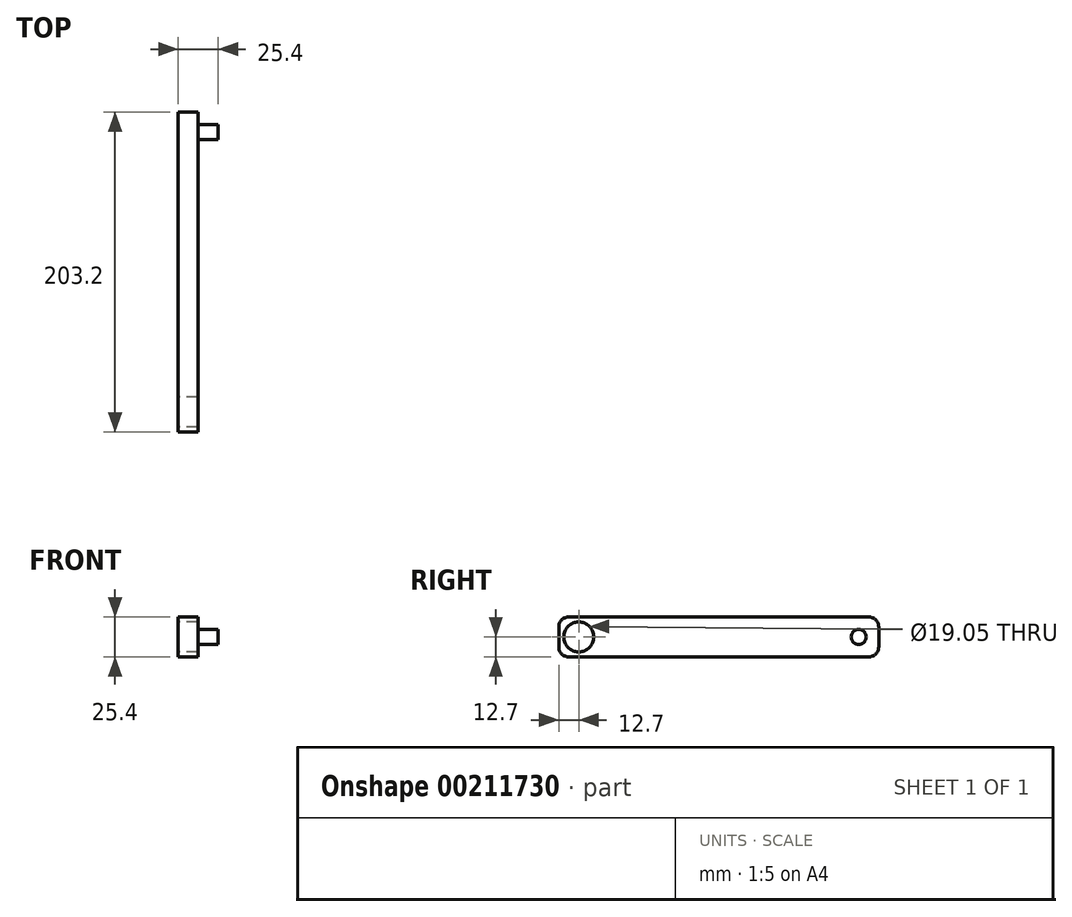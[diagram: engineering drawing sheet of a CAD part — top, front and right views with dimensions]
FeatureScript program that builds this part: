
annotation { "Feature Type Name" : "Feature", "Feature Type Description" : "" }
export const myFeature = defineFeature(function(context is Context, id is Id, definition is map)
    precondition{}
    {
        {
            var Q0;
            Q0=qCreatedBy(makeId("Right.planeOp"),FACE);
            var sketch = newSketch(context, id + "F0", { "sketchPlane" : qUnion([Q0])});
            skLineSegment(sketch, "E0.bottom", {"start": v(95.25, 12.7) * mm, "end": v(-95.25, 12.7) * mm});
            skLineSegment(sketch, "E0.top", {"start": v(95.25, -12.7) * mm, "end": v(-95.25, -12.7) * mm});
            skLineSegment(sketch, "E0.left", {"start": v(101.6, 6.35) * mm, "end": v(101.6, -6.35) * mm});
            skLineSegment(sketch, "E0.right", {"start": v(-101.6, 6.35) * mm, "end": v(-101.6, -6.35) * mm});
            skPoint(sketch, "E0.middle", {"position": v(0, 0) * mm});
            skCircle(sketch, "E1", {"center": v(-88.9, 0) * mm, "radius": 9.53 * mm});
            skPoint(sketch, "E2.visualSharp", {"position": v(-101.6, 12.7) * mm});
            skArc(sketch, "E2.filletArc", {"start": v(-95.25, 12.7) * mm, "mid": v(-99.74, 10.84) * mm, "end": v(-101.6, 6.35) * mm});
            skPoint(sketch, "E3.visualSharp", {"position": v(-101.6, -12.7) * mm});
            skArc(sketch, "E3.filletArc", {"start": v(-101.6, -6.35) * mm, "mid": v(-99.74, -10.84) * mm, "end": v(-95.25, -12.7) * mm});
            skPoint(sketch, "E4.visualSharp", {"position": v(101.6, -12.7) * mm});
            skArc(sketch, "E4.filletArc", {"start": v(95.25, -12.7) * mm, "mid": v(99.74, -10.84) * mm, "end": v(101.6, -6.35) * mm});
            skPoint(sketch, "E5.visualSharp", {"position": v(101.6, 12.7) * mm});
            skArc(sketch, "E5.filletArc", {"start": v(101.6, 6.35) * mm, "mid": v(99.74, 10.84) * mm, "end": v(95.25, 12.7) * mm});
            skSolve(sketch);
        }
        {
            var Q0;
            Q0=makeQuery(id+"F0.imprint","IMPRINT",FACE,{"disambiguationData":[TD([[makeQuery(id+"F0.imprint","IMPRINT",EDGE,{"derivedFrom":sQuery(id+"F0.wireOp",EDGE,"E0.bottom")}),1.0]])]});
            extrude(context, id + "F1", {"entities" : qUnion([Q0]), "endBound" : BoundingType.SYMMETRIC, "depth" : 12.7 * mm});
        }
        {
            var Q0;
            Q0=makeQuery(id+"F1.opExtrude","CAP_FACE",FACE,{"disambiguationData":[OSD([sQuery(id+"F0.wireOp",EDGE,"E0.bottom"),sQuery(id+"F0.wireOp",EDGE,"E0.top"),sQuery(id+"F0.wireOp",EDGE,"E0.left"),sQuery(id+"F0.wireOp",EDGE,"E0.right"),sQuery(id+"F0.wireOp",EDGE,"E1"),sQuery(id+"F0.wireOp",EDGE,"E2.filletArc"),sQuery(id+"F0.wireOp",EDGE,"E3.filletArc"),sQuery(id+"F0.wireOp",EDGE,"E4.filletArc"),sQuery(id+"F0.wireOp",EDGE,"E5.filletArc")])],"isStart":false});
            var sketch = newSketch(context, id + "F2", { "sketchPlane" : qUnion([Q0])});
            skCircle(sketch, "E6", {"center": v(88.9, 0) * mm, "radius": 4.76 * mm});
            skSolve(sketch);
        }
        {
            var Q0;
            Q0=makeQuery(id+"F2.imprint","IMPRINT",FACE,{"disambiguationData":[TD([[makeQuery(id+"F2.imprint","IMPRINT",EDGE,{"derivedFrom":sQuery(id+"F2.wireOp",EDGE,"E6")}),1.0]])]});
            extrude(context, id + "F3", {"entities" : qUnion([Q0]), "operationType" : NewBodyOperationType.ADD, "depth" : 12.7 * mm});
        }
    });
